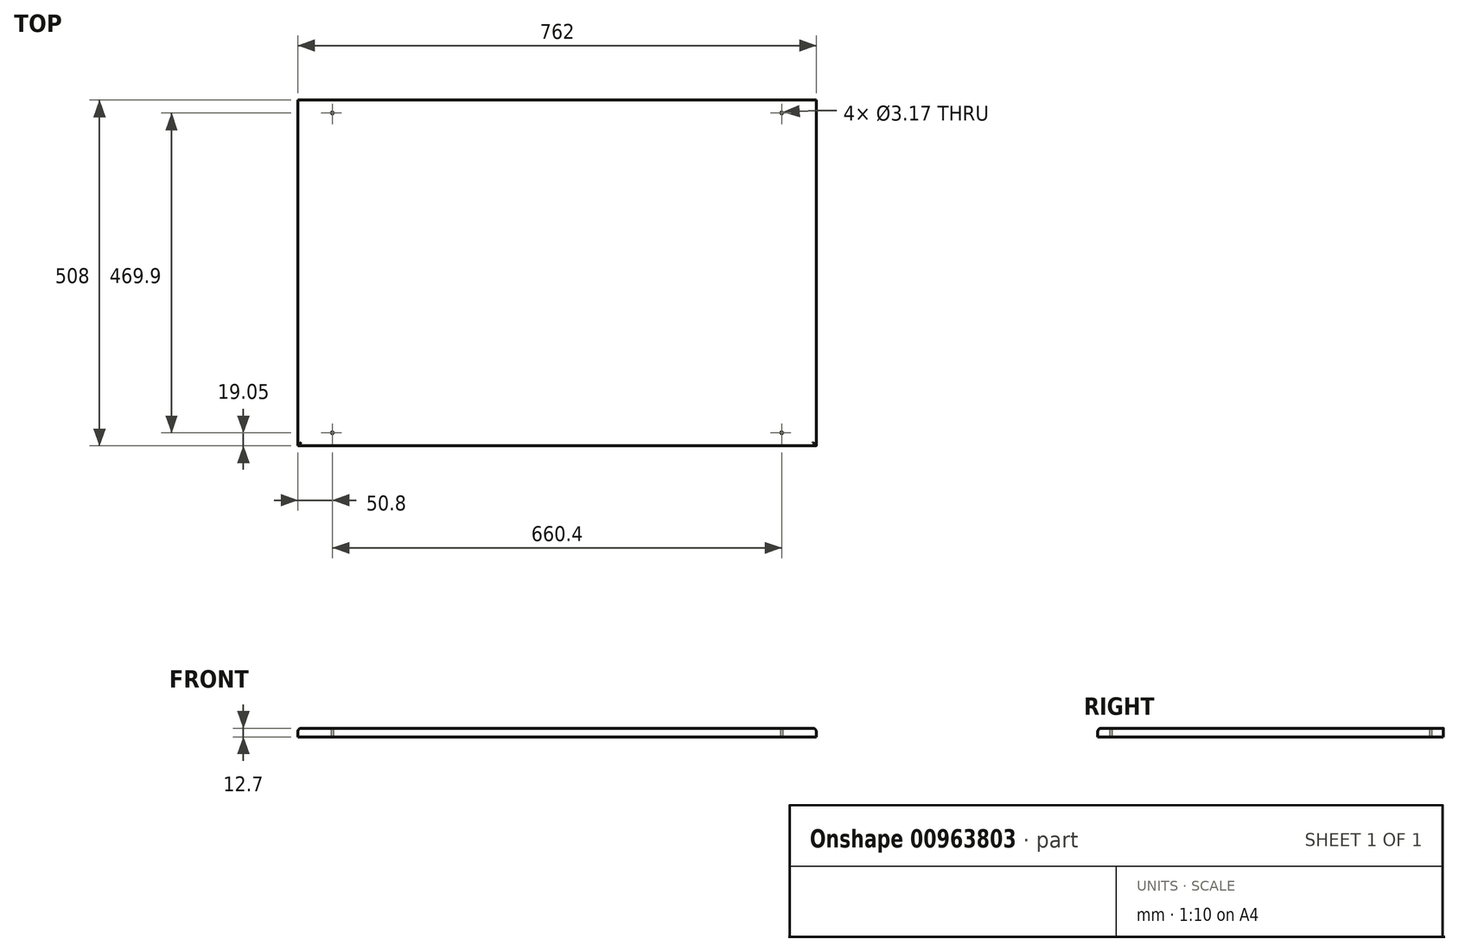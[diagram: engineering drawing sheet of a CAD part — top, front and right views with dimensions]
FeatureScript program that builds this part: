
annotation { "Feature Type Name" : "Feature", "Feature Type Description" : "" }
export const myFeature = defineFeature(function(context is Context, id is Id, definition is map)
    precondition{}
    {
        {
            var Q0;
            Q0=qCreatedBy(makeId("Top.planeOp"),FACE);
            var sketch = newSketch(context, id + "F0", { "sketchPlane" : qUnion([Q0])});
            skLineSegment(sketch, "E0.bottom", {"start": v(381, 254) * mm, "end": v(-381, 254) * mm});
            skLineSegment(sketch, "E0.top", {"start": v(381, -254) * mm, "end": v(-381, -254) * mm});
            skLineSegment(sketch, "E0.left", {"start": v(381, 254) * mm, "end": v(381, -254) * mm});
            skLineSegment(sketch, "E0.right", {"start": v(-381, 254) * mm, "end": v(-381, -254) * mm});
            skPoint(sketch, "E0.middle", {"position": v(0, 0) * mm});
            skSolve(sketch);
        }
        {
            var Q0;
            Q0=makeQuery(id+"F0.imprint","IMPRINT",FACE,{"disambiguationData":[TD([[makeQuery(id+"F0.imprint","IMPRINT",EDGE,{"derivedFrom":sQuery(id+"F0.wireOp",EDGE,"E0.bottom")}),1.0]])]});
            extrude(context, id + "F1", {"entities" : qUnion([Q0]), "oppositeDirection" : true, "depth" : 12.7 * mm, "offsetDistance" : 25.4 * mm});
        }
        {
            var Q0;
            Q0=makeQuery(id+"F1.opExtrude","CAP_EDGE",EDGE,{"disambiguationData":[OSD([sQuery(id+"F0.wireOp",EDGE,"E0.top")])],"isStart":true});
            var Q1;
            {var subQ0=sQuery(id+"F0.wireOp",EDGE,"E0.left");var subQ1=sQuery(id+"F0.wireOp",EDGE,"E0.top");Q1=makeQuery(id+"Fg1MTIqwboO9OPH_1.opFillet","BLEND_EDGE",EDGE,{"blendedFrom":[makeQuery(id+"F1.opExtrude","SWEPT_EDGE",EDGE,{"disambiguationData":[OSD([subQ1,subQ0])]}),makeQuery(id+"F1.opExtrude","CAP_FACE",FACE,{"disambiguationData":[OSD([sQuery(id+"F0.wireOp",EDGE,"E0.bottom"),subQ1,subQ0,sQuery(id+"F0.wireOp",EDGE,"E0.right")])],"isStart":true})],"blendedInto":[makeQuery(id+"F1.opExtrude","CAP_FACE",FACE,{"disambiguationData":[OSD([sQuery(id+"F0.wireOp",EDGE,"E0.bottom"),subQ1,subQ0,sQuery(id+"F0.wireOp",EDGE,"E0.right")])],"isStart":true})]});}
            var Q2;
            Q2=makeQuery(id+"F1.opExtrude","CAP_EDGE",EDGE,{"disambiguationData":[OSD([sQuery(id+"F0.wireOp",EDGE,"E0.left")])],"isStart":true});
            var Q3;
            Q3=makeQuery(id+"F1.opExtrude","CAP_EDGE",EDGE,{"disambiguationData":[OSD([sQuery(id+"F0.wireOp",EDGE,"E0.right")])],"isStart":true});
            var Q4;
            {var subQ0=sQuery(id+"F0.wireOp",EDGE,"E0.right");var subQ1=sQuery(id+"F0.wireOp",EDGE,"E0.top");Q4=makeQuery(id+"Fg1MTIqwboO9OPH_1.opFillet","BLEND_EDGE",EDGE,{"blendedFrom":[makeQuery(id+"F1.opExtrude","SWEPT_EDGE",EDGE,{"disambiguationData":[OSD([subQ1,subQ0])]}),makeQuery(id+"F1.opExtrude","CAP_FACE",FACE,{"disambiguationData":[OSD([sQuery(id+"F0.wireOp",EDGE,"E0.bottom"),subQ1,sQuery(id+"F0.wireOp",EDGE,"E0.left"),subQ0])],"isStart":true})],"blendedInto":[makeQuery(id+"F1.opExtrude","CAP_FACE",FACE,{"disambiguationData":[OSD([sQuery(id+"F0.wireOp",EDGE,"E0.bottom"),subQ1,sQuery(id+"F0.wireOp",EDGE,"E0.left"),subQ0])],"isStart":true})]});}
            fillet(context, id + "F2", {"entities" : qUnion([Q0, Q1, Q2, Q3, Q4]), "radius" : 5.08 * mm, "tangentPropagation" : true, "allowEdgeOverflow" : false});
        }
        {
            var Q0;
            Q0=makeQuery(id+"F1.opExtrude","CAP_FACE",FACE,{"disambiguationData":[OSD([sQuery(id+"F0.wireOp",EDGE,"E0.bottom"),sQuery(id+"F0.wireOp",EDGE,"E0.top"),sQuery(id+"F0.wireOp",EDGE,"E0.left"),sQuery(id+"F0.wireOp",EDGE,"E0.right")])],"isStart":false});
            var sketch = newSketch(context, id + "F3", { "sketchPlane" : qUnion([Q0])});
            skCircle(sketch, "E1", {"center": v(-751.87, 239.2) * mm, "radius": 6.19 * mm});
            skCircle(sketch, "E2", {"center": v(330.2, 234.95) * mm, "radius": 1.59 * mm});
            skSolve(sketch);
        }
        {
            var Q0;
            Q0=makeQuery(id+"F3.imprint","IMPRINT",FACE,{"disambiguationData":[TD([[makeQuery(id+"F3.imprint","IMPRINT",EDGE,{"derivedFrom":sQuery(id+"F3.wireOp",EDGE,"E2")}),1.0]])]});
            var Q1;
            Q1=makeQuery(id+"F1.opExtrude","CAP_FACE",FACE,{"disambiguationData":[OSD([sQuery(id+"F0.wireOp",EDGE,"E0.bottom"),sQuery(id+"F0.wireOp",EDGE,"E0.top"),sQuery(id+"F0.wireOp",EDGE,"E0.left"),sQuery(id+"F0.wireOp",EDGE,"E0.right")])],"isStart":true});
            extrude(context, id + "F4", {"entities" : qUnion([Q0]), "operationType" : NewBodyOperationType.REMOVE, "endBound" : BoundingType.UP_TO_SURFACE, "oppositeDirection" : true, "depth" : 25.4 * mm, "endBoundEntityFace" : qUnion([Q1]), "offsetDistance" : 25.4 * mm});
        }
        {
            var Q0;
            Q0=makeQuery(id+"F1.opExtrude","CAP_FACE",FACE,{"disambiguationData":[OSD([sQuery(id+"F0.wireOp",EDGE,"E0.bottom"),sQuery(id+"F0.wireOp",EDGE,"E0.top"),sQuery(id+"F0.wireOp",EDGE,"E0.left"),sQuery(id+"F0.wireOp",EDGE,"E0.right")])],"isStart":false});
            var sketch = newSketch(context, id + "F5", { "sketchPlane" : qUnion([Q0])});
            skCircle(sketch, "E3", {"center": v(-330.2, 234.95) * mm, "radius": 1.59 * mm});
            skSolve(sketch);
        }
        {
            var Q0;
            Q0=makeQuery(id+"F5.imprint","IMPRINT",FACE,{"disambiguationData":[TD([[makeQuery(id+"F5.imprint","IMPRINT",EDGE,{"derivedFrom":sQuery(id+"F5.wireOp",EDGE,"E3")}),1.0]])]});
            var Q1;
            Q1=sQuery(id+"F5.wireOp",EDGE,"E3");
            var Q2;
            Q2=makeQuery(id+"F1.opExtrude","CAP_FACE",FACE,{"disambiguationData":[OSD([sQuery(id+"F0.wireOp",EDGE,"E0.bottom"),sQuery(id+"F0.wireOp",EDGE,"E0.top"),sQuery(id+"F0.wireOp",EDGE,"E0.left"),sQuery(id+"F0.wireOp",EDGE,"E0.right")])],"isStart":true});
            extrude(context, id + "F6", {"entities" : qUnion([Q0]), "operationType" : NewBodyOperationType.REMOVE, "surfaceEntities" : qUnion([Q1]), "endBound" : BoundingType.UP_TO_SURFACE, "oppositeDirection" : true, "depth" : 25.4 * mm, "endBoundEntityFace" : qUnion([Q2]), "offsetDistance" : 25.4 * mm});
        }
        {
            var Q0;
            Q0=makeQuery(id+"F1.opExtrude","CAP_FACE",FACE,{"disambiguationData":[OSD([sQuery(id+"F0.wireOp",EDGE,"E0.bottom"),sQuery(id+"F0.wireOp",EDGE,"E0.top"),sQuery(id+"F0.wireOp",EDGE,"E0.left"),sQuery(id+"F0.wireOp",EDGE,"E0.right")])],"isStart":false});
            var sketch = newSketch(context, id + "F7", { "sketchPlane" : qUnion([Q0])});
            skCircle(sketch, "E4", {"center": v(330.2, -234.95) * mm, "radius": 1.59 * mm});
            skSolve(sketch);
        }
        {
            var Q0;
            Q0=makeQuery(id+"F7.imprint","IMPRINT",FACE,{"disambiguationData":[TD([[makeQuery(id+"F7.imprint","IMPRINT",EDGE,{"derivedFrom":sQuery(id+"F7.wireOp",EDGE,"E4")}),1.0]])]});
            var Q1;
            Q1=makeQuery(id+"F1.opExtrude","CAP_FACE",FACE,{"disambiguationData":[OSD([sQuery(id+"F0.wireOp",EDGE,"E0.bottom"),sQuery(id+"F0.wireOp",EDGE,"E0.top"),sQuery(id+"F0.wireOp",EDGE,"E0.left"),sQuery(id+"F0.wireOp",EDGE,"E0.right")])],"isStart":true});
            extrude(context, id + "F8", {"entities" : qUnion([Q0]), "operationType" : NewBodyOperationType.REMOVE, "endBound" : BoundingType.UP_TO_SURFACE, "oppositeDirection" : true, "depth" : 25.4 * mm, "endBoundEntityFace" : qUnion([Q1]), "offsetDistance" : 25.4 * mm});
        }
        {
            var Q0;
            Q0=makeQuery(id+"F1.opExtrude","CAP_FACE",FACE,{"disambiguationData":[OSD([sQuery(id+"F0.wireOp",EDGE,"E0.bottom"),sQuery(id+"F0.wireOp",EDGE,"E0.top"),sQuery(id+"F0.wireOp",EDGE,"E0.left"),sQuery(id+"F0.wireOp",EDGE,"E0.right")])],"isStart":false});
            var sketch = newSketch(context, id + "F9", { "sketchPlane" : qUnion([Q0])});
            skCircle(sketch, "E5", {"center": v(-330.2, -234.95) * mm, "radius": 1.59 * mm});
            skSolve(sketch);
        }
        {
            var Q0;
            Q0=makeQuery(id+"F9.imprint","IMPRINT",FACE,{"disambiguationData":[TD([[makeQuery(id+"F9.imprint","IMPRINT",EDGE,{"derivedFrom":sQuery(id+"F9.wireOp",EDGE,"E5")}),1.0]])]});
            var Q1;
            Q1=makeQuery(id+"F1.opExtrude","CAP_FACE",FACE,{"disambiguationData":[OSD([sQuery(id+"F0.wireOp",EDGE,"E0.bottom"),sQuery(id+"F0.wireOp",EDGE,"E0.top"),sQuery(id+"F0.wireOp",EDGE,"E0.left"),sQuery(id+"F0.wireOp",EDGE,"E0.right")])],"isStart":true});
            extrude(context, id + "F10", {"entities" : qUnion([Q0]), "operationType" : NewBodyOperationType.REMOVE, "endBound" : BoundingType.UP_TO_SURFACE, "oppositeDirection" : true, "depth" : 25.4 * mm, "endBoundEntityFace" : qUnion([Q1]), "offsetDistance" : 25.4 * mm});
        }
    });
